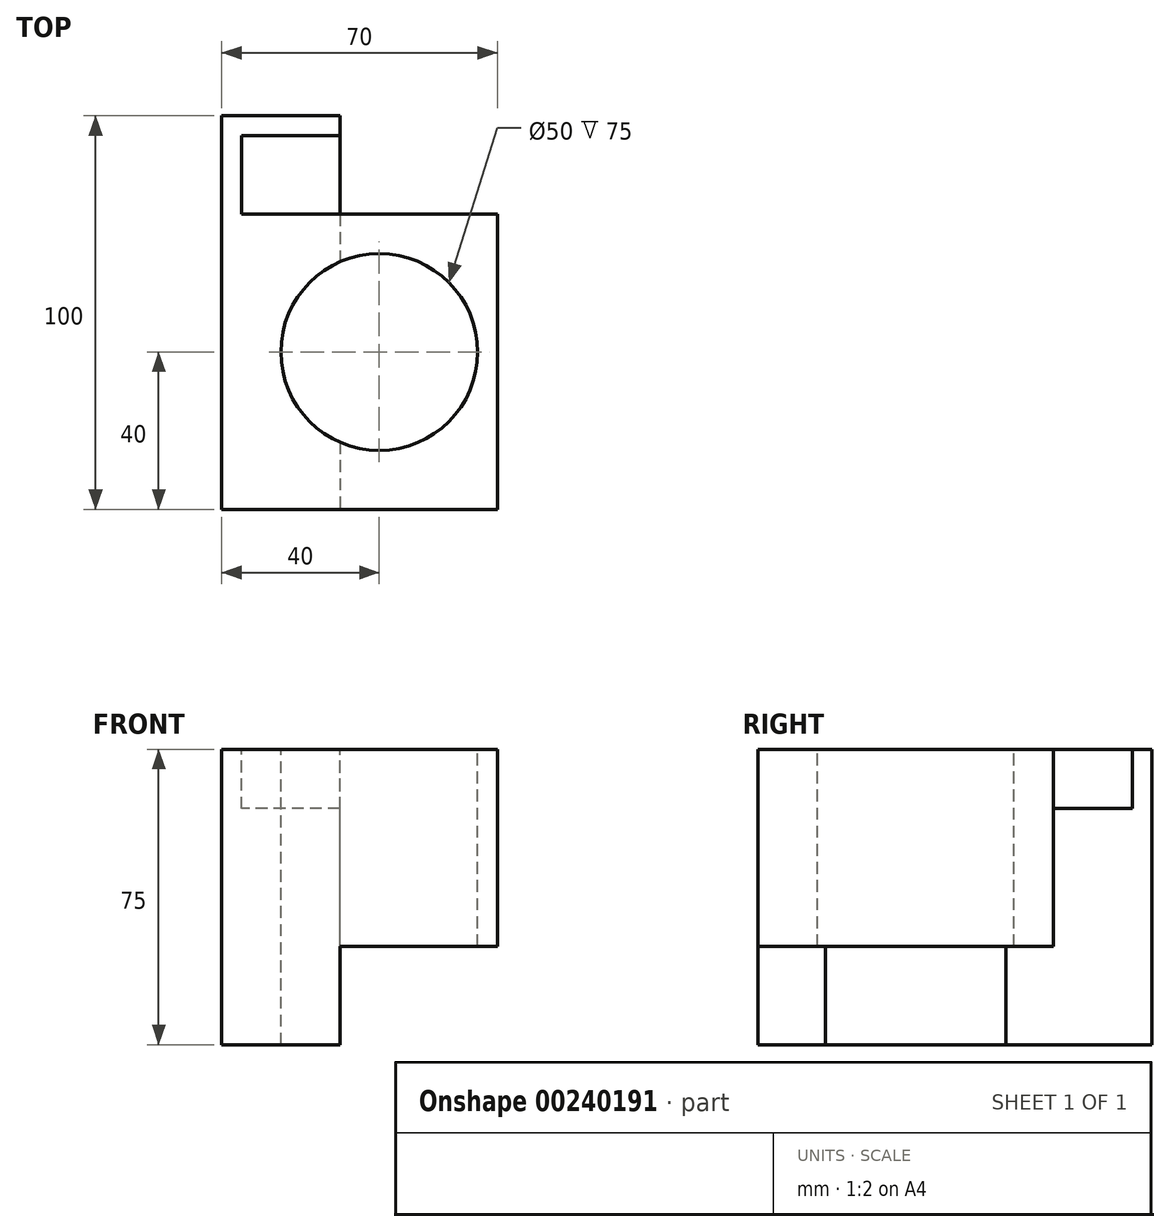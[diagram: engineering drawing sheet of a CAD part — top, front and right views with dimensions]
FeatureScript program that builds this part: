
annotation { "Feature Type Name" : "Feature", "Feature Type Description" : "" }
export const myFeature = defineFeature(function(context is Context, id is Id, definition is map)
    precondition{}
    {
        {
            var Q0;
            Q0=qCreatedBy(makeId("Front.planeOp"),FACE);
            var sketch = newSketch(context, id + "F0", { "sketchPlane" : qUnion([Q0])});
            skLineSegment(sketch, "E0.bottom", {"start": v(0, 0) * mm, "end": v(70, 0) * mm});
            skLineSegment(sketch, "E0.top", {"start": v(0, 75) * mm, "end": v(70, 75) * mm});
            skLineSegment(sketch, "E0.left", {"start": v(0, 0) * mm, "end": v(0, 75) * mm});
            skLineSegment(sketch, "E0.right", {"start": v(70, 0) * mm, "end": v(70, 75) * mm});
            skSolve(sketch);
        }
        {
            var Q0;
            Q0 = qSketchRegion(id + "F0", true);
            extrude(context, id + "F1", {"entities" : qUnion([Q0]), "oppositeDirection" : true, "depth" : 100 * mm});
        }
        {
            var Q0;
            Q0=makeQuery(id+"F1.opExtrude","CAP_FACE",FACE,{"disambiguationData":[OSD([sQuery(id+"F0.wireOp",EDGE,"E0.bottom"),sQuery(id+"F0.wireOp",EDGE,"E0.top"),sQuery(id+"F0.wireOp",EDGE,"E0.left"),sQuery(id+"F0.wireOp",EDGE,"E0.right")])],"isStart":true});
            var sketch = newSketch(context, id + "F2", { "sketchPlane" : qUnion([Q0])});
            skLineSegment(sketch, "E1.bottom", {"start": v(30, 0) * mm, "end": v(70, 0) * mm});
            skLineSegment(sketch, "E1.top", {"start": v(30, 25) * mm, "end": v(70, 25) * mm});
            skLineSegment(sketch, "E1.left", {"start": v(30, 0) * mm, "end": v(30, 25) * mm});
            skLineSegment(sketch, "E1.right", {"start": v(70, 0) * mm, "end": v(70, 25) * mm});
            skSolve(sketch);
        }
        {
            var Q0;
            Q0 = qSketchRegion(id + "F2", true);
            extrude(context, id + "F3", {"entities" : qUnion([Q0]), "operationType" : NewBodyOperationType.REMOVE, "endBound" : BoundingType.THROUGH_ALL, "oppositeDirection" : true, "depth" : 25 * mm});
        }
        {
            var Q0;
            Q0=makeQuery(id+"F1.opExtrude","SWEPT_FACE",FACE,{"disambiguationData":[OSD([sQuery(id+"F0.wireOp",EDGE,"E0.top")])]});
            var sketch = newSketch(context, id + "F4", { "sketchPlane" : qUnion([Q0])});
            skLineSegment(sketch, "E2.bottom", {"start": v(30, 75) * mm, "end": v(70, 75) * mm});
            skLineSegment(sketch, "E2.top", {"start": v(30, 100) * mm, "end": v(70, 100) * mm});
            skLineSegment(sketch, "E2.left", {"start": v(30, 75) * mm, "end": v(30, 100) * mm});
            skLineSegment(sketch, "E2.right", {"start": v(70, 75) * mm, "end": v(70, 100) * mm});
            skSolve(sketch);
        }
        {
            var Q0;
            Q0 = qSketchRegion(id + "F4", true);
            extrude(context, id + "F5", {"entities" : qUnion([Q0]), "operationType" : NewBodyOperationType.REMOVE, "endBound" : BoundingType.THROUGH_ALL, "oppositeDirection" : true, "depth" : 25 * mm});
        }
        {
            var Q0;
            Q0=makeQuery(id+"F1.opExtrude","SWEPT_FACE",FACE,{"disambiguationData":[OSD([sQuery(id+"F0.wireOp",EDGE,"E0.top")])]});
            var sketch = newSketch(context, id + "F6", { "sketchPlane" : qUnion([Q0])});
            skCircle(sketch, "E3", {"center": v(40, 40) * mm, "radius": 25 * mm});
            skSolve(sketch);
        }
        {
            var Q0;
            Q0 = qSketchRegion(id + "F6", true);
            extrude(context, id + "F7", {"entities" : qUnion([Q0]), "operationType" : NewBodyOperationType.REMOVE, "endBound" : BoundingType.THROUGH_ALL, "oppositeDirection" : true, "depth" : 25 * mm});
        }
        {
            var Q0;
            Q0=makeQuery(id+"F1.opExtrude","SWEPT_FACE",FACE,{"disambiguationData":[OSD([sQuery(id+"F0.wireOp",EDGE,"E0.top")])]});
            var sketch = newSketch(context, id + "F8", { "sketchPlane" : qUnion([Q0])});
            skLineSegment(sketch, "E4.bottom", {"start": v(30, 75) * mm, "end": v(5, 75) * mm});
            skLineSegment(sketch, "E4.top", {"start": v(30, 95) * mm, "end": v(5, 95) * mm});
            skLineSegment(sketch, "E4.left", {"start": v(30, 75) * mm, "end": v(30, 95) * mm});
            skLineSegment(sketch, "E4.right", {"start": v(5, 75) * mm, "end": v(5, 95) * mm});
            skSolve(sketch);
        }
        {
            var Q0;
            Q0 = qSketchRegion(id + "F8", true);
            extrude(context, id + "F9", {"entities" : qUnion([Q0]), "operationType" : NewBodyOperationType.REMOVE, "oppositeDirection" : true, "depth" : 15 * mm});
        }
    });
